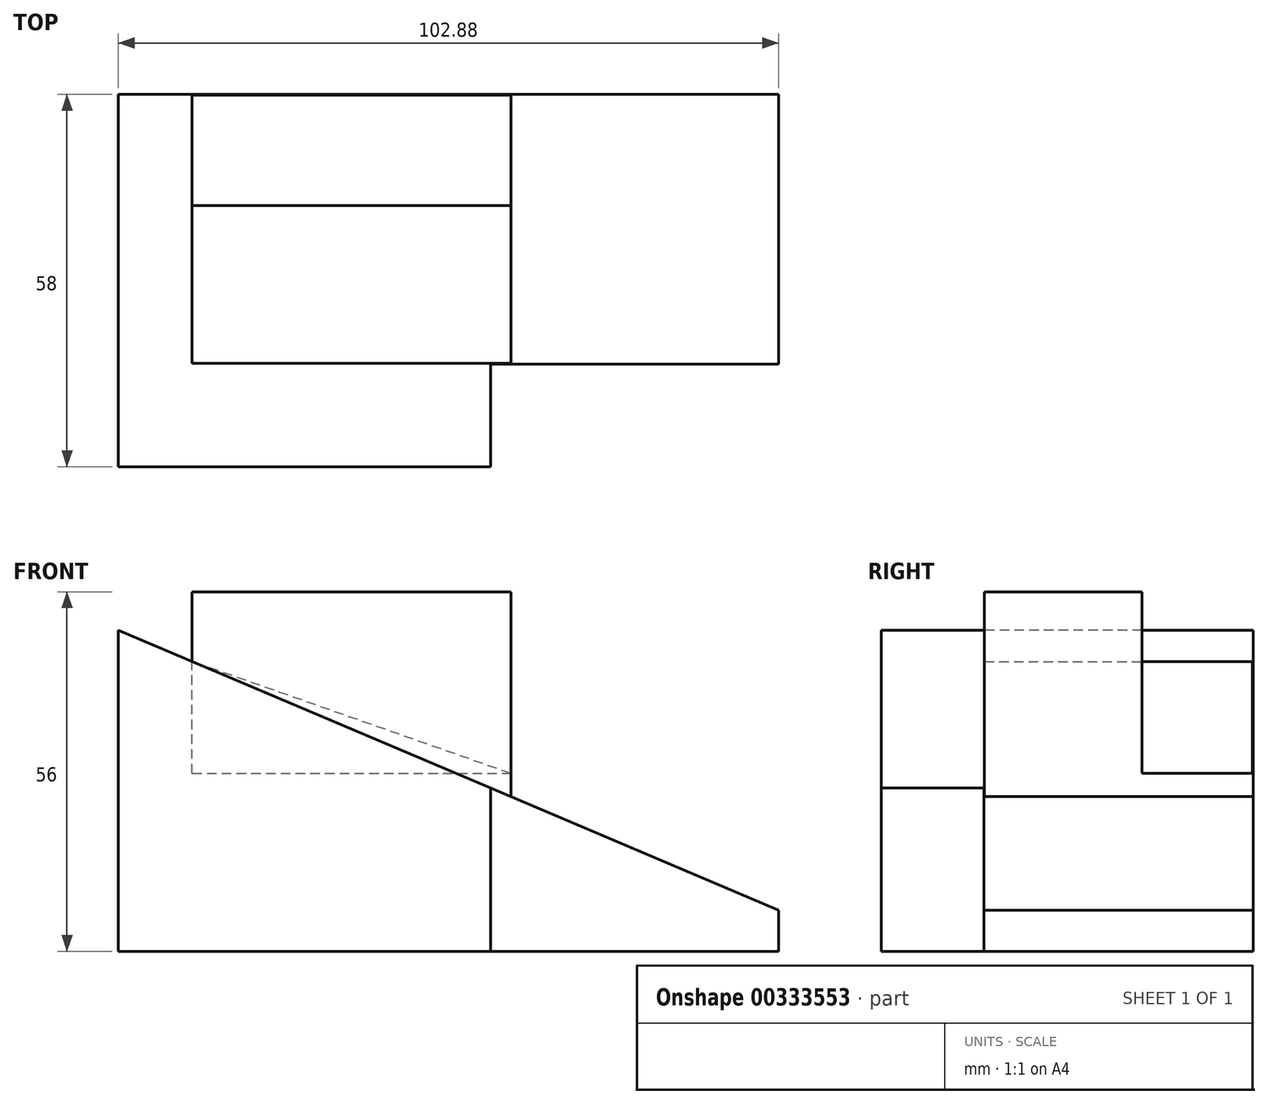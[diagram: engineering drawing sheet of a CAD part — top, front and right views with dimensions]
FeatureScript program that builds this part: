
annotation { "Feature Type Name" : "Feature", "Feature Type Description" : "" }
export const myFeature = defineFeature(function(context is Context, id is Id, definition is map)
    precondition{}
    {
        {
            var Q0;
            Q0=qCreatedBy(makeId("Top.planeOp"),FACE);
            var sketch = newSketch(context, id + "F0", { "sketchPlane" : qUnion([Q0])});
            skLineSegment(sketch, "E0", {"start": v(0, 58) * mm, "end": v(0, 0) * mm});
            skLineSegment(sketch, "E1", {"start": v(0, 0) * mm, "end": v(58, 0) * mm});
            skLineSegment(sketch, "E2", {"start": v(58, 0) * mm, "end": v(58, 16) * mm});
            skLineSegment(sketch, "E3", {"start": v(58, 16) * mm, "end": v(102.88, 16) * mm});
            skLineSegment(sketch, "E4", {"start": v(102.88, 16) * mm, "end": v(102.88, 58) * mm});
            skLineSegment(sketch, "E5", {"start": v(102.88, 58) * mm, "end": v(0, 58) * mm});
            skLineSegment(sketch, "E6.bottom", {"start": v(88, 16) * mm, "end": v(16, 16) * mm});
            skLineSegment(sketch, "E6.top", {"start": v(88, 42) * mm, "end": v(16, 42) * mm});
            skLineSegment(sketch, "E6.left", {"start": v(88, 16) * mm, "end": v(88, 42) * mm});
            skLineSegment(sketch, "E6.right", {"start": v(16, 16) * mm, "end": v(16, 42) * mm});
            skSolve(sketch);
        }
        {
            var Q0;
            Q0=makeQuery(id+"F0.imprint","IMPRINT",FACE,{"disambiguationData":[TD([[makeQuery(id+"F0.imprint","IMPRINT",EDGE,{"derivedFrom":sQuery(id+"F0.wireOp",EDGE,"E0")}),1.0]])]});
            var Q1;
            Q1=makeQuery(id+"F0.imprint","IMPRINT",FACE,{"disambiguationData":[TD([[makeQuery(id+"F0.imprint","IMPRINT",EDGE,{"derivedFrom":sQuery(id+"F0.wireOp",EDGE,"E6.top")}),1.0]])]});
            extrude(context, id + "F1", {"entities" : qUnion([Q0, Q1]), "depth" : 50 * mm});
        }
        {
            var Q0;
            Q0=makeQuery(id+"F1.opExtrude","SWEPT_FACE",FACE,{"disambiguationData":[OSD([sQuery(id+"F0.wireOp",EDGE,"E1")])]});
            var sketch = newSketch(context, id + "F2", { "sketchPlane" : qUnion([Q0])});
            skLineSegment(sketch, "E7", {"start": v(0, 50) * mm, "end": v(118, 0) * mm});
            skLineSegment(sketch, "E8", {"start": v(0, 50) * mm, "end": v(102.9, 50) * mm});
            skLineSegment(sketch, "E9", {"start": v(102.9, 50) * mm, "end": v(118, 0) * mm});
            skSolve(sketch);
        }
        {
            var Q0;
            {var subQ1=sQuery(id+"F2.wireOp",EDGE,"E7");var subQ2=sQuery(id+"F0.wireOp",EDGE,"E1");var subQ4=makeQuery(id+"F1.opExtrude","SWEPT_EDGE",EDGE,{"disambiguationData":[OSD([subQ2,sQuery(id+"F0.wireOp",EDGE,"E2")])]});var subQ5=makeQuery(id+"F2.imprint","INTERSECT",VERTEX,{"derivedFrom":[subQ4,subQ1]});Q0=makeQuery(id+"F2.imprint","IMPRINT",FACE,{"disambiguationData":[TD([[makeQuery(id+"F2.imprint","IMPRINT",EDGE,{"disambiguationData":[TD([[subQ5,1.0]])],"derivedFrom":subQ1}),1.0]])]});}
            var Q1;
            {var subQ0=sQuery(id+"F2.wireOp",EDGE,"E9");Q1=makeQuery(id+"F2.imprint","IMPRINT",FACE,{"disambiguationData":[TD([[makeQuery(id+"F2.imprint","IMPRINT",EDGE,{"derivedFrom":subQ0}),-1.0]])]});}
            var Q2;
            Q2=sQuery(id+"F2.wireOp",EDGE,"E7");
            var Q3;
            Q3=sQuery(id+"F2.wireOp",EDGE,"E9");
            var Q4;
            Q4=sQuery(id+"F2.wireOp",EDGE,"E8");
            extrude(context, id + "F3", {"entities" : qUnion([Q0, Q1]), "operationType" : NewBodyOperationType.REMOVE, "surfaceEntities" : qUnion([Q2, Q3, Q4]), "oppositeDirection" : true, "depth" : 81.2 * mm});
        }
        {
            var Q0;
            {var subQ0=sQuery(id+"F2.wireOp",EDGE,"E9");Q0=makeQuery(id+"F2.imprint","IMPRINT",FACE,{"disambiguationData":[TD([[makeQuery(id+"F2.imprint","IMPRINT",EDGE,{"derivedFrom":subQ0}),-1.0]])]});}
            extrude(context, id + "F4", {"entities" : qUnion([Q0]), "operationType" : NewBodyOperationType.REMOVE, "oppositeDirection" : true, "depth" : 25 * mm});
        }
        {
            var Q0;
            Q0=makeQuery(id+"F1.opExtrude","SWEPT_FACE",FACE,{"disambiguationData":[OSD([sQuery(id+"F0.wireOp",EDGE,"E5")])]});
            var sketch = newSketch(context, id + "F5", { "sketchPlane" : qUnion([Q0])});
            skLineSegment(sketch, "E10.bottom", {"start": v(-61.16, 0) * mm, "end": v(-11.5, 0) * mm});
            skLineSegment(sketch, "E10.top", {"start": v(-61.16, 56) * mm, "end": v(-11.5, 56) * mm});
            skLineSegment(sketch, "E10.left", {"start": v(-61.16, 0) * mm, "end": v(-61.16, 56) * mm});
            skLineSegment(sketch, "E10.right", {"start": v(-11.5, 0) * mm, "end": v(-11.5, 56) * mm});
            skSolve(sketch);
        }
        {
            var Q0;
            Q0 = qSketchRegion(id + "F5", true);
            extrude(context, id + "F6", {"entities" : qUnion([Q0]), "operationType" : NewBodyOperationType.ADD, "oppositeDirection" : true, "depth" : 41.9 * mm});
        }
        {
            var Q0;
            Q0=makeQuery(id+"F6.opExtrude","SWEPT_FACE",FACE,{"disambiguationData":[OSD([sQuery(id+"F5.wireOp",EDGE,"E10.top")])]});
            var sketch = newSketch(context, id + "F7", { "sketchPlane" : qUnion([Q0])});
            skLineSegment(sketch, "E11.bottom", {"start": v(11.5, 40.68) * mm, "end": v(61.16, 40.68) * mm});
            skLineSegment(sketch, "E11.top", {"start": v(11.5, 58) * mm, "end": v(61.16, 58) * mm});
            skLineSegment(sketch, "E11.left", {"start": v(11.5, 40.68) * mm, "end": v(11.5, 58) * mm});
            skLineSegment(sketch, "E11.right", {"start": v(61.16, 40.68) * mm, "end": v(61.16, 58) * mm});
            skSolve(sketch);
        }
        {
            var Q0;
            Q0=makeQuery(id+"F7.imprint","IMPRINT",FACE,{"disambiguationData":[TD([[makeQuery(id+"F7.imprint","IMPRINT",EDGE,{"derivedFrom":sQuery(id+"F7.wireOp",EDGE,"E11.bottom")}),1.0]])]});
            extrude(context, id + "F8", {"entities" : qUnion([Q0]), "operationType" : NewBodyOperationType.REMOVE, "oppositeDirection" : true, "depth" : 28.3 * mm});
        }
        {
            var Q0;
            Q0=makeQuery(id+"F8.boolean.opBoolean","COPY",FACE,{"derivedFrom":makeQuery(id+"F8.opExtrude","SWEPT_FACE",FACE,{"disambiguationData":[OSD([sQuery(id+"F7.wireOp",EDGE,"E11.bottom")])]})});
            var sketch = newSketch(context, id + "F9", { "sketchPlane" : qUnion([Q0])});
            skLineSegment(sketch, "E12", {"start": v(-61.16, 27.7) * mm, "end": v(-11.5, 45.13) * mm});
            skLineSegment(sketch, "E13", {"start": v(-11.5, 45.13) * mm, "end": v(-11.5, 27.7) * mm});
            skLineSegment(sketch, "E14", {"start": v(-11.5, 27.7) * mm, "end": v(-61.16, 27.7) * mm});
            skSolve(sketch);
        }
        {
            var Q0;
            Q0 = qSketchRegion(id + "F9", true);
            extrude(context, id + "F10", {"entities" : qUnion([Q0]), "operationType" : NewBodyOperationType.ADD, "depth" : 17.2 * mm});
        }
    });
